# Revit family: Sanitary_Showers_DURAVIT-AG_Shower-rail-100x70x700-mm-UV0600003ed
name_source: partatom
category: Generic Models
revit_build: Autodesk Revit 2018 (Build: 20190510_1515(x64)
units: mm (PartAtom-declared; Revit-internal decimal feet)

## family parameters
Can host rebar = No
Cut with Voids When Loaded = No
Host = Face
OmniClass Number = 23.31.17.00
OmniClass Title = Showers
Part Type = Normal
Room Calculation Point = No
Round Connector Dimension = Use Diameter
Shared = No

## types (2) — shared parameters
BIMobject category = Showers
Default Elevation = 1219 mm
Design country = Germany
ETIM classification = EC010140 | Sliding rod
Edition number = 1
IFC Classification = Sanitary Terminal
Installation instructions = https://pro.duravit.com
Manufacturer = Duravit
Manufacturer country = Germany
Manufacturer name = DURAVIT AG
Masterformat 2014 Code = 22 41 23
Masterformat 2014 Description = Residential Showers
Material main = Brass
Material secondary = Plastic
Model = Shower rail 100x70x700 mm - UV0600003
OmniClass Code = 23-31 17 00
OmniClass Description = Showers
Product Guid = c63dcc17-abd7-4481-94a6-3b069ae790aa
Product SKU = Shower-rail-100x70x700-mm-UV0600003
Product certification = https://pro.duravit.com
Product data url = https://bimobject.com
Product family = Universal
Product group = Hand shower
Product name = Shower rail 100x70x700 mm - UV0600003
Product url = https://pro.duravit.com
QR code = https://bimobject.com
Technical description = https://pro.duravit.com
UNSPSC Code = 30181503
URL = https://www.duravit.com
Uniclass 2015 Code = SL_35_80_80
Uniclass 2015 Name = Showers
Uniformat II Code = D2010
Uniformat II Description = Plumbing Fixtures
Weight Net (Kg) = 0.335
Youtube clip = https://pro.duravit.com

## per-type parameters (varying)
| type | Description | Main material |
| 46 - Black Matt | Duravit Shower rail Black Matt 100x70x700 mm - UV0600003046 | Duravit - Metal - 46 - Black Matt |
| 10 - Chrome | Duravit Shower rail Chrome High Gloss 100x70x700 mm - UV0600003010 | Duravit - Metal - 10 - Chrome |

## geometry (parser evidence)
native form markers: Sweep x3
no freeform markers — native parametric forms only
